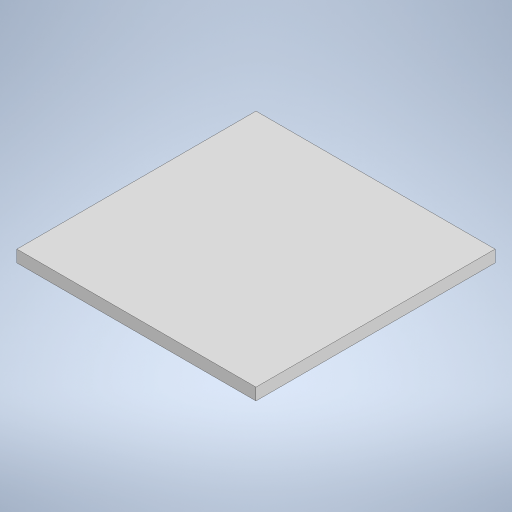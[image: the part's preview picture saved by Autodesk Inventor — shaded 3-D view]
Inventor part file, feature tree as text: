
AUTODESK INVENTOR PART (.ipt)
format: ipt  version: 2024.2 (Build 282272000, 272)  size: 198,144 bytes
history: native  units: in
note: dims shown in document units (in); Inventor stores cm internally (conversion verified against a paired STEP export)
features: extrude x1, sketch x1
ambient origin geometry x8: Origin, YZ Plane, XZ Plane, XY Plane, X Axis, Y Axis, Z Axis, Center Point
bodies: Solid1 (feature_tree)
feature tree (2):
  extrude  "Extrusion1"  Depth=5.0in
  sketch  "Sketch1"  dims[d0=5.0in d1=5.0in d2=0.25in d3=0.0in]
